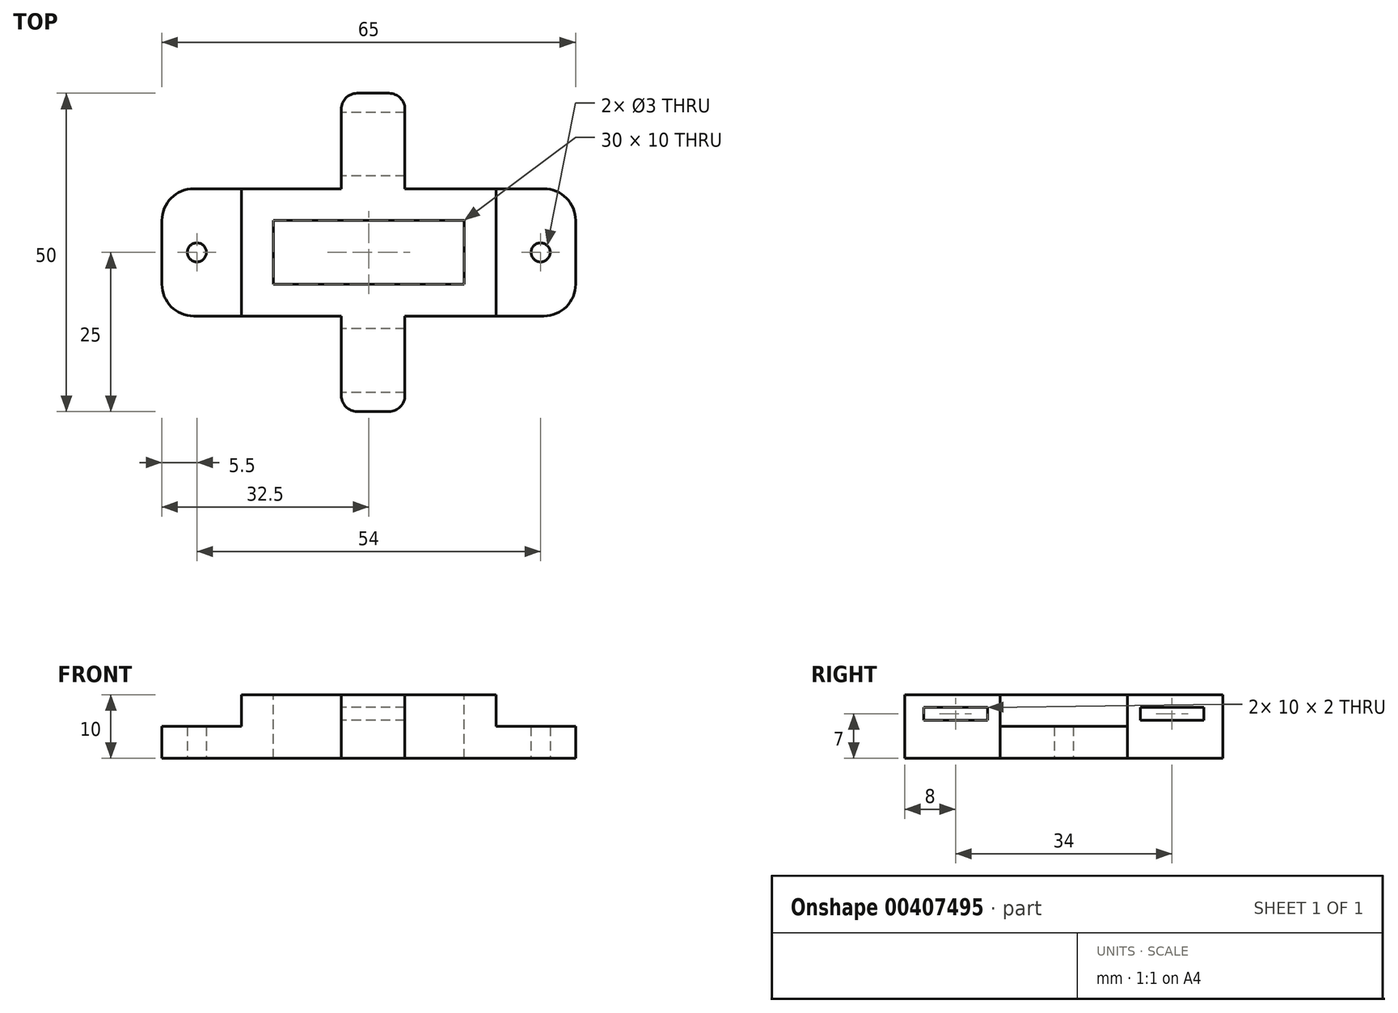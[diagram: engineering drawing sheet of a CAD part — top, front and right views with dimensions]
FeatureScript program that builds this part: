
annotation { "Feature Type Name" : "Feature", "Feature Type Description" : "" }
export const myFeature = defineFeature(function(context is Context, id is Id, definition is map)
    precondition{}
    {
        {
            var Q0;
            Q0=qCreatedBy(makeId("Top.planeOp"),FACE);
            var sketch = newSketch(context, id + "F0", { "sketchPlane" : qUnion([Q0])});
            skLineSegment(sketch, "E0.bottom", {"start": v(32.5, 10) * mm, "end": v(-32.5, 10) * mm});
            skLineSegment(sketch, "E0.top", {"start": v(32.5, -10) * mm, "end": v(-32.5, -10) * mm});
            skLineSegment(sketch, "E0.left", {"start": v(32.5, 10) * mm, "end": v(32.5, -10) * mm});
            skLineSegment(sketch, "E0.right", {"start": v(-32.5, 10) * mm, "end": v(-32.5, -10) * mm});
            skPoint(sketch, "E0.middle", {"position": v(0, 0) * mm});
            skCircle(sketch, "E1", {"center": v(-27, 0) * mm, "radius": 1.5 * mm});
            skCircle(sketch, "E2", {"center": v(27, 0) * mm, "radius": 1.5 * mm});
            skLineSegment(sketch, "E3.bottom", {"start": v(5.68, 25) * mm, "end": v(-4.32, 25) * mm});
            skLineSegment(sketch, "E3.top", {"start": v(5.68, -25) * mm, "end": v(-4.32, -25) * mm});
            skLineSegment(sketch, "E3.left", {"start": v(5.68, 25) * mm, "end": v(5.68, -25) * mm});
            skLineSegment(sketch, "E3.right", {"start": v(-4.32, 25) * mm, "end": v(-4.32, -25) * mm});
            skPoint(sketch, "E3.middle", {"position": v(0.68, 0) * mm});
            skSolve(sketch);
        }
        {
            var Q0;
            Q0=makeQuery(id+"F0.imprint","IMPRINT",FACE,{"disambiguationData":[TD([[makeQuery(id+"F0.imprint","IMPRINT",EDGE,{"derivedFrom":sQuery(id+"F0.wireOp",EDGE,"E0.bottom")}),1.0]])]});
            var Q1;
            {var subQ0=sQuery(id+"F0.wireOp",EDGE,"E0.right");Q1=makeQuery(id+"F0.imprint","IMPRINT",FACE,{"disambiguationData":[TD([[makeQuery(id+"F0.imprint","IMPRINT",EDGE,{"derivedFrom":subQ0}),1.0]])]});}
            var Q2;
            {var subQ0=sQuery(id+"F0.wireOp",EDGE,"E0.left");Q2=makeQuery(id+"F0.imprint","IMPRINT",FACE,{"disambiguationData":[TD([[makeQuery(id+"F0.imprint","IMPRINT",EDGE,{"derivedFrom":subQ0}),-1.0]])]});}
            var Q3;
            {var subQ5=sQuery(id+"F0.wireOp",EDGE,"E3.bottom");Q3=makeQuery(id+"F0.imprint","IMPRINT",FACE,{"disambiguationData":[TD([[makeQuery(id+"F0.imprint","IMPRINT",EDGE,{"derivedFrom":subQ5}),1.0]])]});}
            var Q4;
            {var subQ5=sQuery(id+"F0.wireOp",EDGE,"E3.top");Q4=makeQuery(id+"F0.imprint","IMPRINT",FACE,{"disambiguationData":[TD([[makeQuery(id+"F0.imprint","IMPRINT",EDGE,{"derivedFrom":subQ5}),-1.0]])]});}
            extrude(context, id + "F1", {"entities" : qUnion([Q0, Q1, Q2, Q3, Q4]), "depth" : 5 * mm});
        }
        {
            var Q0;
            Q0=makeQuery(id+"F1.opExtrude","CAP_FACE",FACE,{"disambiguationData":[OSD([sQuery(id+"F0.wireOp",EDGE,"E0.bottom"),sQuery(id+"F0.wireOp",EDGE,"E0.top"),sQuery(id+"F0.wireOp",EDGE,"E0.left"),sQuery(id+"F0.wireOp",EDGE,"E0.right"),sQuery(id+"F0.wireOp",EDGE,"E1"),sQuery(id+"F0.wireOp",EDGE,"E2"),sQuery(id+"F0.wireOp",EDGE,"E3.bottom"),sQuery(id+"F0.wireOp",EDGE,"E3.top"),sQuery(id+"F0.wireOp",EDGE,"E3.left"),sQuery(id+"F0.wireOp",EDGE,"E3.right")])],"isStart":false});
            var sketch = newSketch(context, id + "F2", { "sketchPlane" : qUnion([Q0])});
            skLineSegment(sketch, "E4.bottom", {"start": v(20, 10) * mm, "end": v(-20, 10) * mm});
            skLineSegment(sketch, "E4.top", {"start": v(20, -10) * mm, "end": v(-20, -10) * mm});
            skLineSegment(sketch, "E4.left", {"start": v(20, 10) * mm, "end": v(20, -10) * mm});
            skLineSegment(sketch, "E4.right", {"start": v(-20, 10) * mm, "end": v(-20, -10) * mm});
            skPoint(sketch, "E4.middle", {"position": v(0, 0) * mm});
            skSolve(sketch);
        }
        {
            var Q0;
            Q0 = qSketchRegion(id + "F2", true);
            var Q1;
            {var subQ2=sQuery(id+"F0.wireOp",EDGE,"E3.bottom");Q1=makeQuery(id+"F2.imprint","IMPRINT",FACE,{"disambiguationData":[TD([[makeQuery(id+"F2.imprint","IMPRINT",EDGE,{"derivedFrom":makeQuery(id+"F1.opExtrude","CAP_EDGE",EDGE,{"disambiguationData":[OSD([subQ2])],"isStart":false})}),1.0]])]});}
            var Q2;
            {var subQ2=sQuery(id+"F0.wireOp",EDGE,"E3.top");Q2=makeQuery(id+"F2.imprint","IMPRINT",FACE,{"disambiguationData":[TD([[makeQuery(id+"F2.imprint","IMPRINT",EDGE,{"derivedFrom":makeQuery(id+"F1.opExtrude","CAP_EDGE",EDGE,{"disambiguationData":[OSD([subQ2])],"isStart":false})}),-1.0]])]});}
            extrude(context, id + "F3", {"entities" : qUnion([Q0, Q1, Q2]), "operationType" : NewBodyOperationType.ADD, "depth" : 5 * mm});
        }
        {
            var Q0;
            {var subQ0=sQuery(id+"F0.wireOp",EDGE,"E3.right");var subQ1=makeQuery(id+"F0.imprint","IMPRINT",EDGE,{"disambiguationData":[TD([[makeQuery(id+"F0.imprint","INTERSECT",VERTEX,{"derivedFrom":[sQuery(id+"F0.wireOp",EDGE,"E3.bottom"),subQ0]}),-1.0]])],"derivedFrom":subQ0});Q0=makeQuery(id+"F3.boolean.opBoolean","MERGE",FACE,{"derivedFrom":[makeQuery(id+"F1.opExtrude","SWEPT_FACE",FACE,{"disambiguationData":[OSD([subQ0]),TDD([subQ1])]}),makeQuery(id+"F3.opExtrude","SWEPT_FACE",FACE,{"disambiguationData":[OSD([subQ0]),TDD([makeQuery(id+"F2.imprint","IMPRINT",EDGE,{"derivedFrom":makeQuery(id+"F1.opExtrude","CAP_EDGE",EDGE,{"disambiguationData":[OSD([subQ0]),TDD([subQ1])],"isStart":false})})])]})]});}
            var sketch = newSketch(context, id + "F4", { "sketchPlane" : qUnion([Q0])});
            skLineSegment(sketch, "E5.bottom", {"start": v(-22, 8) * mm, "end": v(-12, 8) * mm});
            skLineSegment(sketch, "E5.top", {"start": v(-22, 6) * mm, "end": v(-12, 6) * mm});
            skLineSegment(sketch, "E5.left", {"start": v(-22, 8) * mm, "end": v(-22, 6) * mm});
            skLineSegment(sketch, "E5.right", {"start": v(-12, 8) * mm, "end": v(-12, 6) * mm});
            skLineSegment(sketch, "E6.bottom", {"start": v(12, 8) * mm, "end": v(22, 8) * mm});
            skLineSegment(sketch, "E6.top", {"start": v(12, 6) * mm, "end": v(22, 6) * mm});
            skLineSegment(sketch, "E6.left", {"start": v(12, 8) * mm, "end": v(12, 6) * mm});
            skLineSegment(sketch, "E6.right", {"start": v(22, 8) * mm, "end": v(22, 6) * mm});
            skSolve(sketch);
        }
        {
            var Q0;
            Q0=makeQuery(id+"F4.imprint","IMPRINT",FACE,{"disambiguationData":[TD([[makeQuery(id+"F4.imprint","IMPRINT",EDGE,{"derivedFrom":sQuery(id+"F4.wireOp",EDGE,"E5.bottom")}),-1.0]])]});
            var Q1;
            Q1=makeQuery(id+"F4.imprint","IMPRINT",FACE,{"disambiguationData":[TD([[makeQuery(id+"F4.imprint","IMPRINT",EDGE,{"derivedFrom":sQuery(id+"F4.wireOp",EDGE,"E6.bottom")}),-1.0]])]});
            extrude(context, id + "F5", {"entities" : qUnion([Q0, Q1]), "operationType" : NewBodyOperationType.REMOVE, "oppositeDirection" : true, "depth" : 10 * mm});
        }
        {
            var Q0;
            Q0=makeQuery(id+"F3.opExtrude","CAP_FACE",FACE,{"disambiguationData":[OSD([sQuery(id+"F0.wireOp",EDGE,"E3.bottom"),sQuery(id+"F0.wireOp",EDGE,"E3.top"),sQuery(id+"F0.wireOp",EDGE,"E3.left"),sQuery(id+"F0.wireOp",EDGE,"E3.right"),sQuery(id+"F2.wireOp",EDGE,"E4.bottom"),sQuery(id+"F2.wireOp",EDGE,"E4.top"),sQuery(id+"F2.wireOp",EDGE,"E4.left"),sQuery(id+"F2.wireOp",EDGE,"E4.right")])],"isStart":false});
            var sketch = newSketch(context, id + "F6", { "sketchPlane" : qUnion([Q0])});
            skLineSegment(sketch, "E7.bottom", {"start": v(15, 5) * mm, "end": v(-15, 5) * mm});
            skLineSegment(sketch, "E7.top", {"start": v(15, -5) * mm, "end": v(-15, -5) * mm});
            skLineSegment(sketch, "E7.left", {"start": v(15, 5) * mm, "end": v(15, -5) * mm});
            skLineSegment(sketch, "E7.right", {"start": v(-15, 5) * mm, "end": v(-15, -5) * mm});
            skPoint(sketch, "E7.middle", {"position": v(0, 0) * mm});
            skSolve(sketch);
        }
        {
            var Q0;
            Q0=makeQuery(id+"F6.imprint","IMPRINT",FACE,{"disambiguationData":[TD([[makeQuery(id+"F6.imprint","IMPRINT",EDGE,{"derivedFrom":sQuery(id+"F6.wireOp",EDGE,"E7.bottom")}),1.0]])]});
            extrude(context, id + "F7", {"entities" : qUnion([Q0]), "operationType" : NewBodyOperationType.REMOVE, "oppositeDirection" : true, "depth" : 25 * mm});
        }
        {
            var Q0;
            Q0=makeQuery(id+"F1.opExtrude","SWEPT_EDGE",EDGE,{"disambiguationData":[OSD([sQuery(id+"F0.wireOp",EDGE,"E0.top"),sQuery(id+"F0.wireOp",EDGE,"E0.right")])]});
            var Q1;
            Q1=makeQuery(id+"F1.opExtrude","SWEPT_EDGE",EDGE,{"disambiguationData":[OSD([sQuery(id+"F0.wireOp",EDGE,"E0.bottom"),sQuery(id+"F0.wireOp",EDGE,"E0.right")])]});
            var Q2;
            Q2=makeQuery(id+"F1.opExtrude","SWEPT_EDGE",EDGE,{"disambiguationData":[OSD([sQuery(id+"F0.wireOp",EDGE,"E0.bottom"),sQuery(id+"F0.wireOp",EDGE,"E0.left")])]});
            var Q3;
            Q3=makeQuery(id+"F1.opExtrude","SWEPT_EDGE",EDGE,{"disambiguationData":[OSD([sQuery(id+"F0.wireOp",EDGE,"E0.top"),sQuery(id+"F0.wireOp",EDGE,"E0.left")])]});
            fillet(context, id + "F8", {"entities" : qUnion([Q0, Q1, Q2, Q3]), "radius" : 5 * mm, "tangentPropagation" : true, "allowEdgeOverflow" : false});
        }
        {
            var Q0;
            {var subQ0=sQuery(id+"F0.wireOp",EDGE,"E3.right");var subQ1=sQuery(id+"F0.wireOp",EDGE,"E3.top");Q0=makeQuery(id+"F3.boolean.opBoolean","MERGE",EDGE,{"derivedFrom":[makeQuery(id+"F1.opExtrude","SWEPT_EDGE",EDGE,{"disambiguationData":[OSD([subQ1,subQ0])]}),makeQuery(id+"F3.opExtrude","SWEPT_EDGE",EDGE,{"disambiguationData":[OSD([subQ1,subQ0])]})]});}
            var Q1;
            {var subQ0=sQuery(id+"F0.wireOp",EDGE,"E3.left");var subQ1=sQuery(id+"F0.wireOp",EDGE,"E3.top");Q1=makeQuery(id+"F3.boolean.opBoolean","MERGE",EDGE,{"derivedFrom":[makeQuery(id+"F1.opExtrude","SWEPT_EDGE",EDGE,{"disambiguationData":[OSD([subQ1,subQ0])]}),makeQuery(id+"F3.opExtrude","SWEPT_EDGE",EDGE,{"disambiguationData":[OSD([subQ1,subQ0])]})]});}
            var Q2;
            {var subQ0=sQuery(id+"F0.wireOp",EDGE,"E3.left");var subQ1=sQuery(id+"F0.wireOp",EDGE,"E3.bottom");Q2=makeQuery(id+"F3.boolean.opBoolean","MERGE",EDGE,{"derivedFrom":[makeQuery(id+"F1.opExtrude","SWEPT_EDGE",EDGE,{"disambiguationData":[OSD([subQ1,subQ0])]}),makeQuery(id+"F3.opExtrude","SWEPT_EDGE",EDGE,{"disambiguationData":[OSD([subQ1,subQ0])]})]});}
            var Q3;
            {var subQ0=sQuery(id+"F0.wireOp",EDGE,"E3.right");var subQ1=sQuery(id+"F0.wireOp",EDGE,"E3.bottom");Q3=makeQuery(id+"F3.boolean.opBoolean","MERGE",EDGE,{"derivedFrom":[makeQuery(id+"F1.opExtrude","SWEPT_EDGE",EDGE,{"disambiguationData":[OSD([subQ1,subQ0])]}),makeQuery(id+"F3.opExtrude","SWEPT_EDGE",EDGE,{"disambiguationData":[OSD([subQ1,subQ0])]})]});}
            fillet(context, id + "F9", {"entities" : qUnion([Q0, Q1, Q2, Q3]), "radius" : 2.5 * mm, "tangentPropagation" : true, "allowEdgeOverflow" : false});
        }
    });
